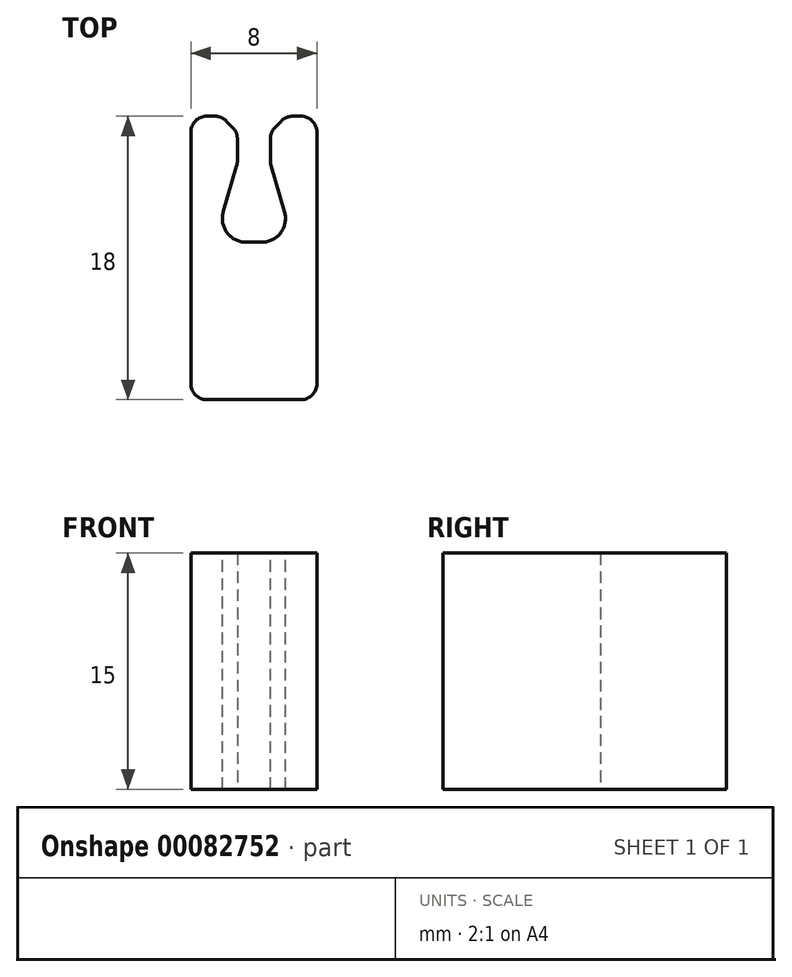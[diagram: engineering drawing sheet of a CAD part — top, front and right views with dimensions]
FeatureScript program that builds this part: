
annotation { "Feature Type Name" : "Feature", "Feature Type Description" : "" }
export const myFeature = defineFeature(function(context is Context, id is Id, definition is map)
    precondition{}
    {
        {
            var Q0;
            Q0=qCreatedBy(makeId("Top.planeOp"),FACE);
            var sketch = newSketch(context, id + "F0", { "sketchPlane" : qUnion([Q0])});
            skLineSegment(sketch, "E0", {"start": v(-2.5, 10) * mm, "end": v(-1.05, 15) * mm});
            skLineSegment(sketch, "E1", {"start": v(-1.05, 15) * mm, "end": v(-1.05, 18) * mm});
            skLineSegment(sketch, "E2", {"start": v(-1.05, 18) * mm, "end": v(-4, 18) * mm});
            skLineSegment(sketch, "E3", {"start": v(-4, 18) * mm, "end": v(-4, 0) * mm});
            skLineSegment(sketch, "E4", {"start": v(-4, 0) * mm, "end": v(4, 0) * mm});
            skLineSegment(sketch, "E5", {"start": v(4, 0) * mm, "end": v(4, 18) * mm});
            skLineSegment(sketch, "E6", {"start": v(4, 18) * mm, "end": v(1.05, 18) * mm});
            skLineSegment(sketch, "E7", {"start": v(1.05, 18) * mm, "end": v(1.05, 15) * mm});
            skLineSegment(sketch, "E8", {"start": v(1.05, 15) * mm, "end": v(2.5, 10) * mm});
            skLineSegment(sketch, "E9", {"start": v(2.5, 10) * mm, "end": v(-2.5, 10) * mm});
            skLineSegment(sketch, "E10", {"start": v(-1.05, 18) * mm, "end": v(1.05, 18) * mm, "construction": true});
            skLineSegment(sketch, "E11", {"start": v(-1.05, 15) * mm, "end": v(1.05, 15) * mm, "construction": true});
            skPoint(sketch, "E12", {"position": v(0, 18) * mm});
            skPoint(sketch, "E13", {"position": v(0, 15) * mm});
            skPoint(sketch, "E14", {"position": v(0, 10) * mm});
            skPoint(sketch, "E15", {"position": v(0, 0) * mm});
            skSolve(sketch);
        }
        {
            var Q0;
            Q0=makeQuery(id+"F0.imprint","IMPRINT",FACE,{"disambiguationData":[TD([[makeQuery(id+"F0.imprint","IMPRINT",EDGE,{"derivedFrom":sQuery(id+"F0.wireOp",EDGE,"E0")}),1.0]])]});
            extrude(context, id + "F1", {"entities" : qUnion([Q0]), "depth" : 15 * mm});
        }
        {
            var Q0;
            Q0=makeQuery(id+"F1.opExtrude","SWEPT_EDGE",EDGE,{"disambiguationData":[OSD([sQuery(id+"F0.wireOp",EDGE,"E1"),sQuery(id+"F0.wireOp",EDGE,"E2")])]});
            var Q1;
            Q1=makeQuery(id+"F1.opExtrude","SWEPT_EDGE",EDGE,{"disambiguationData":[OSD([sQuery(id+"F0.wireOp",EDGE,"E6"),sQuery(id+"F0.wireOp",EDGE,"E7")])]});
            chamfer(context, id + "F2", {"entities" : qUnion([Q0, Q1]), "width" : 1 * mm, "tangentPropagation" : true});
        }
        {
            var Q0;
            Q0=makeQuery(id+"F1.opExtrude","SWEPT_EDGE",EDGE,{"disambiguationData":[OSD([sQuery(id+"F0.wireOp",EDGE,"E0"),sQuery(id+"F0.wireOp",EDGE,"E9")])]});
            var Q1;
            Q1=makeQuery(id+"F1.opExtrude","SWEPT_EDGE",EDGE,{"disambiguationData":[OSD([sQuery(id+"F0.wireOp",EDGE,"E8"),sQuery(id+"F0.wireOp",EDGE,"E9")])]});
            fillet(context, id + "F3", {"entities" : qUnion([Q0, Q1]), "radius" : 1.5 * mm, "tangentPropagation" : true, "allowEdgeOverflow" : false});
        }
        {
            var Q0;
            Q0=makeQuery(id+"F1.opExtrude","SWEPT_EDGE",EDGE,{"disambiguationData":[OSD([sQuery(id+"F0.wireOp",EDGE,"E0"),sQuery(id+"F0.wireOp",EDGE,"E1")])]});
            var Q1;
            {var subQ0=sQuery(id+"F0.wireOp",EDGE,"E1");Q1=makeQuery(id+"F2.opChamfer","BLEND_EDGE",EDGE,{"blendedFrom":[makeQuery(id+"F1.opExtrude","SWEPT_EDGE",EDGE,{"disambiguationData":[OSD([subQ0,sQuery(id+"F0.wireOp",EDGE,"E2")])]}),makeQuery(id+"F1.opExtrude","SWEPT_FACE",FACE,{"disambiguationData":[OSD([subQ0])]})],"blendedInto":[makeQuery(id+"F1.opExtrude","SWEPT_FACE",FACE,{"disambiguationData":[OSD([subQ0])]})]});}
            var Q2;
            {var subQ0=sQuery(id+"F0.wireOp",EDGE,"E2");Q2=makeQuery(id+"F2.opChamfer","BLEND_EDGE",EDGE,{"blendedFrom":[makeQuery(id+"F1.opExtrude","SWEPT_EDGE",EDGE,{"disambiguationData":[OSD([sQuery(id+"F0.wireOp",EDGE,"E1"),subQ0])]}),makeQuery(id+"F1.opExtrude","SWEPT_FACE",FACE,{"disambiguationData":[OSD([subQ0])]})],"blendedInto":[makeQuery(id+"F1.opExtrude","SWEPT_FACE",FACE,{"disambiguationData":[OSD([subQ0])]})]});}
            var Q3;
            Q3=makeQuery(id+"F1.opExtrude","SWEPT_EDGE",EDGE,{"disambiguationData":[OSD([sQuery(id+"F0.wireOp",EDGE,"E7"),sQuery(id+"F0.wireOp",EDGE,"E8")])]});
            var Q4;
            {var subQ0=sQuery(id+"F0.wireOp",EDGE,"E7");Q4=makeQuery(id+"F2.opChamfer","BLEND_EDGE",EDGE,{"blendedFrom":[makeQuery(id+"F1.opExtrude","SWEPT_EDGE",EDGE,{"disambiguationData":[OSD([sQuery(id+"F0.wireOp",EDGE,"E6"),subQ0])]}),makeQuery(id+"F1.opExtrude","SWEPT_FACE",FACE,{"disambiguationData":[OSD([subQ0])]})],"blendedInto":[makeQuery(id+"F1.opExtrude","SWEPT_FACE",FACE,{"disambiguationData":[OSD([subQ0])]})]});}
            var Q5;
            {var subQ0=sQuery(id+"F0.wireOp",EDGE,"E6");Q5=makeQuery(id+"F2.opChamfer","BLEND_EDGE",EDGE,{"blendedFrom":[makeQuery(id+"F1.opExtrude","SWEPT_EDGE",EDGE,{"disambiguationData":[OSD([subQ0,sQuery(id+"F0.wireOp",EDGE,"E7")])]}),makeQuery(id+"F1.opExtrude","SWEPT_FACE",FACE,{"disambiguationData":[OSD([subQ0])]})],"blendedInto":[makeQuery(id+"F1.opExtrude","SWEPT_FACE",FACE,{"disambiguationData":[OSD([subQ0])]})]});}
            var Q6;
            Q6=makeQuery(id+"F1.opExtrude","SWEPT_EDGE",EDGE,{"disambiguationData":[OSD([sQuery(id+"F0.wireOp",EDGE,"E5"),sQuery(id+"F0.wireOp",EDGE,"E6")])]});
            var Q7;
            Q7=makeQuery(id+"F1.opExtrude","SWEPT_EDGE",EDGE,{"disambiguationData":[OSD([sQuery(id+"F0.wireOp",EDGE,"E2"),sQuery(id+"F0.wireOp",EDGE,"E3")])]});
            var Q8;
            Q8=makeQuery(id+"F1.opExtrude","SWEPT_EDGE",EDGE,{"disambiguationData":[OSD([sQuery(id+"F0.wireOp",EDGE,"E3"),sQuery(id+"F0.wireOp",EDGE,"E4")])]});
            var Q9;
            Q9=makeQuery(id+"F1.opExtrude","SWEPT_EDGE",EDGE,{"disambiguationData":[OSD([sQuery(id+"F0.wireOp",EDGE,"E4"),sQuery(id+"F0.wireOp",EDGE,"E5")])]});
            fillet(context, id + "F4", {"entities" : qUnion([Q0, Q1, Q2, Q3, Q4, Q5, Q6, Q7, Q8, Q9]), "radius" : 1 * mm, "tangentPropagation" : true, "allowEdgeOverflow" : false});
        }
    });
